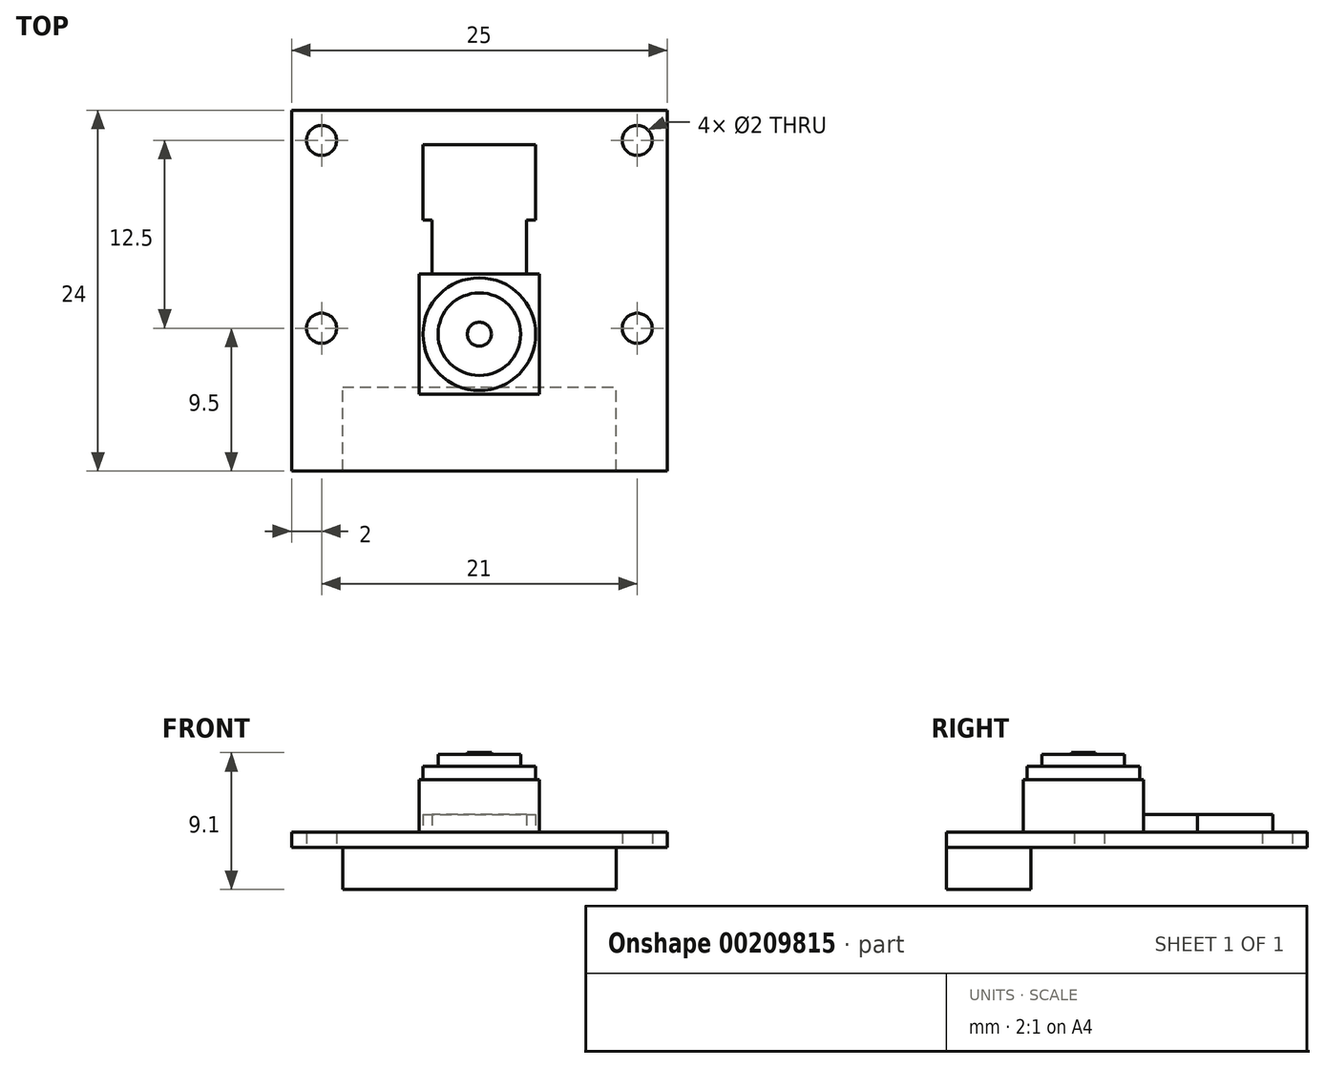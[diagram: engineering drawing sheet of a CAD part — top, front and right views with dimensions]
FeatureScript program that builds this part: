
annotation { "Feature Type Name" : "Feature", "Feature Type Description" : "" }
export const myFeature = defineFeature(function(context is Context, id is Id, definition is map)
    precondition{}
    {
        {
            var Q0;
            Q0=qCreatedBy(makeId("Top.planeOp"),FACE);
            var sketch = newSketch(context, id + "F0", { "sketchPlane" : qUnion([Q0])});
            skLineSegment(sketch, "E0.rect.bottom", {"start": v(12.5, 12) * mm, "end": v(-12.5, 12) * mm});
            skLineSegment(sketch, "E0.rect.top", {"start": v(12.5, -12) * mm, "end": v(-12.5, -12) * mm});
            skLineSegment(sketch, "E0.rect.left", {"start": v(12.5, 12) * mm, "end": v(12.5, -12) * mm});
            skLineSegment(sketch, "E0.rect.right", {"start": v(-12.5, 12) * mm, "end": v(-12.5, -12) * mm});
            skPoint(sketch, "E0.rect.middle", {"position": v(0, 0) * mm});
            skCircle(sketch, "E1", {"center": v(-10.5, 10) * mm, "radius": 1 * mm});
            skCircle(sketch, "E2", {"center": v(-10.5, -2.5) * mm, "radius": 1 * mm});
            skLineSegment(sketch, "E3", {"start": v(-10.5, 10) * mm, "end": v(-10.5, -12) * mm, "construction": true});
            skCircle(sketch, "E4.MirrorC", {"center": v(10.5, 10) * mm, "radius": 1 * mm});
            skCircle(sketch, "E5.MirrorC", {"center": v(10.5, -2.5) * mm, "radius": 1 * mm});
            skSolve(sketch);
        }
        {
            var Q0;
            Q0=makeQuery(id+"F0.imprint","IMPRINT",FACE,{"disambiguationData":[TD([[makeQuery(id+"F0.imprint","IMPRINT",EDGE,{"derivedFrom":sQuery(id+"F0.wireOp",EDGE,"E0.rect.bottom")}),1.0]])]});
            extrude(context, id + "F1", {"entities" : qUnion([Q0]), "depth" : 1 * mm});
        }
        {
            var Q0;
            Q0=makeQuery(id+"F1.opExtrude","CAP_FACE",FACE,{"disambiguationData":[OSD([sQuery(id+"F0.wireOp",EDGE,"E0.rect.bottom"),sQuery(id+"F0.wireOp",EDGE,"E0.rect.top"),sQuery(id+"F0.wireOp",EDGE,"E0.rect.left"),sQuery(id+"F0.wireOp",EDGE,"E0.rect.right"),sQuery(id+"F0.wireOp",EDGE,"E1"),sQuery(id+"F0.wireOp",EDGE,"E2"),sQuery(id+"F0.wireOp",EDGE,"E4.MirrorC"),sQuery(id+"F0.wireOp",EDGE,"E5.MirrorC")])],"isStart":false});
            var sketch = newSketch(context, id + "F2", { "sketchPlane" : qUnion([Q0])});
            skLineSegment(sketch, "E6", {"start": v(-12.5, -2.9) * mm, "end": v(12.5, -2.9) * mm, "construction": true});
            skLineSegment(sketch, "E7.rect.bottom", {"start": v(4, 1.1) * mm, "end": v(-4, 1.1) * mm});
            skLineSegment(sketch, "E7.rect.top", {"start": v(4, -6.9) * mm, "end": v(-4, -6.9) * mm});
            skLineSegment(sketch, "E7.rect.left", {"start": v(4, 1.1) * mm, "end": v(4, -6.9) * mm});
            skLineSegment(sketch, "E7.rect.right", {"start": v(-4, 1.1) * mm, "end": v(-4, -6.9) * mm});
            skPoint(sketch, "E7.rect.middle", {"position": v(0, -2.9) * mm});
            skCircle(sketch, "E8", {"center": v(0, -2.9) * mm, "radius": 3.75 * mm});
            skCircle(sketch, "E9", {"center": v(0, -2.9) * mm, "radius": 2.75 * mm});
            skLineSegment(sketch, "E10.bottom", {"start": v(-3.4, 1.1) * mm, "end": v(3.4, 1.1) * mm});
            skSolve(sketch);
        }
        {
            var Q0;
            Q0=qSketchRegion(id+"F2",true);
            var Q1;
            Q1=makeQuery(id+"F2.imprint","IMPRINT",FACE,{"disambiguationData":[TD([[makeQuery(id+"F2.imprint","IMPRINT",EDGE,{"derivedFrom":sQuery(id+"F2.wireOp",EDGE,"E8")}),1.0]])]});
            var Q2;
            Q2=makeQuery(id+"F2.imprint","IMPRINT",FACE,{"disambiguationData":[TD([[makeQuery(id+"F2.imprint","IMPRINT",EDGE,{"derivedFrom":sQuery(id+"F2.wireOp",EDGE,"E9")}),1.0]])]});
            extrude(context, id + "F3", {"entities" : qUnion([Q0, Q1, Q2]), "depth" : 3.5 * mm});
        }
        {
            var Q0;
            Q0=makeQuery(id+"F2.imprint","IMPRINT",FACE,{"disambiguationData":[TD([[makeQuery(id+"F2.imprint","IMPRINT",EDGE,{"derivedFrom":sQuery(id+"F2.wireOp",EDGE,"E8")}),1.0]])]});
            var Q1;
            Q1=makeQuery(id+"F2.imprint","IMPRINT",FACE,{"disambiguationData":[TD([[makeQuery(id+"F2.imprint","IMPRINT",EDGE,{"derivedFrom":sQuery(id+"F2.wireOp",EDGE,"E9")}),1.0]])]});
            extrude(context, id + "F4", {"entities" : qUnion([Q0, Q1]), "operationType" : NewBodyOperationType.ADD, "depth" : (3.5 + 0.9) * mm});
        }
        {
            var Q0;
            Q0=makeQuery(id+"F2.imprint","IMPRINT",FACE,{"disambiguationData":[TD([[makeQuery(id+"F2.imprint","IMPRINT",EDGE,{"derivedFrom":sQuery(id+"F2.wireOp",EDGE,"E9")}),1.0]])]});
            extrude(context, id + "F5", {"entities" : qUnion([Q0]), "operationType" : NewBodyOperationType.ADD, "depth" : 5.2 * mm});
        }
        {
            var Q0;
            Q0=makeQuery(id+"F5.opExtrude","CAP_FACE",FACE,{"disambiguationData":[OSD([sQuery(id+"F2.wireOp",EDGE,"E9")])],"isStart":false});
            var sketch = newSketch(context, id + "F6", { "sketchPlane" : qUnion([Q0])});
            skCircle(sketch, "E11", {"center": v(0, -2.9) * mm, "radius": 0.8 * mm});
            skSolve(sketch);
        }
        {
            var Q0;
            Q0=makeQuery(id+"F6.imprint","IMPRINT",FACE,{"disambiguationData":[TD([[makeQuery(id+"F6.imprint","IMPRINT",EDGE,{"derivedFrom":sQuery(id+"F6.wireOp",EDGE,"E11")}),1.0]])]});
            extrude(context, id + "F7", {"entities" : qUnion([Q0]), "depth" : 0.1 * mm});
        }
        {
            var Q0;
            Q0=makeQuery(id+"F1.opExtrude","CAP_FACE",FACE,{"disambiguationData":[OSD([sQuery(id+"F0.wireOp",EDGE,"E0.rect.bottom"),sQuery(id+"F0.wireOp",EDGE,"E0.rect.top"),sQuery(id+"F0.wireOp",EDGE,"E0.rect.left"),sQuery(id+"F0.wireOp",EDGE,"E0.rect.right"),sQuery(id+"F0.wireOp",EDGE,"E1"),sQuery(id+"F0.wireOp",EDGE,"E2"),sQuery(id+"F0.wireOp",EDGE,"E4.MirrorC"),sQuery(id+"F0.wireOp",EDGE,"E5.MirrorC")])],"isStart":true});
            var sketch = newSketch(context, id + "F8", { "sketchPlane" : qUnion([Q0])});
            skLineSegment(sketch, "E12.bottom", {"start": v(-9.1, 12) * mm, "end": v(9.1, 12) * mm});
            skLineSegment(sketch, "E12.top", {"start": v(-9.1, 6.4) * mm, "end": v(9.1, 6.4) * mm});
            skLineSegment(sketch, "E12.left", {"start": v(-9.1, 12) * mm, "end": v(-9.1, 6.4) * mm});
            skLineSegment(sketch, "E12.right", {"start": v(9.1, 12) * mm, "end": v(9.1, 6.4) * mm});
            skSolve(sketch);
        }
        {
            var Q0;
            Q0=qSketchRegion(id+"F8",true);
            extrude(context, id + "F9", {"entities" : qUnion([Q0]), "depth" : 2.8 * mm});
        }
        {
            var Q0;
            Q0=makeQuery(id+"F2.imprint","IMPRINT",FACE,{"disambiguationData":[TD([[makeQuery(id+"F2.imprint","IMPRINT",EDGE,{"derivedFrom":sQuery(id+"F2.wireOp",EDGE,"E7.rect.top")}),1.0]])]});
            var sketch = newSketch(context, id + "F10", { "sketchPlane" : qUnion([Q0])});
            skLineSegment(sketch, "E13.bottom", {"start": v(-3.75, 1.1) * mm, "end": v(3.75, 1.1) * mm});
            skLineSegment(sketch, "E13.top", {"start": v(-3.75, 9.7) * mm, "end": v(3.75, 9.7) * mm});
            skLineSegment(sketch, "E13.left", {"start": v(-3.75, 4.7) * mm, "end": v(-3.75, 9.7) * mm});
            skLineSegment(sketch, "E13.right", {"start": v(3.75, 4.7) * mm, "end": v(3.75, 9.7) * mm});
            skLineSegment(sketch, "E14", {"start": v(-3.75, 4.7) * mm, "end": v(-3.15, 4.7) * mm});
            skLineSegment(sketch, "E15", {"start": v(-3.15, 4.7) * mm, "end": v(-3.15, 1.1) * mm});
            skLineSegment(sketch, "E16", {"start": v(3.15, 4.7) * mm, "end": v(3.15, 1.1) * mm});
            skLineSegment(sketch, "E17.trimOffspring", {"start": v(3.15, 4.7) * mm, "end": v(3.75, 4.7) * mm});
            skSolve(sketch);
        }
        {
            var Q0;
            Q0=qSketchRegion(id+"F10",true);
            extrude(context, id + "F11", {"entities" : qUnion([Q0]), "depth" : 1.2 * mm});
        }
    });
